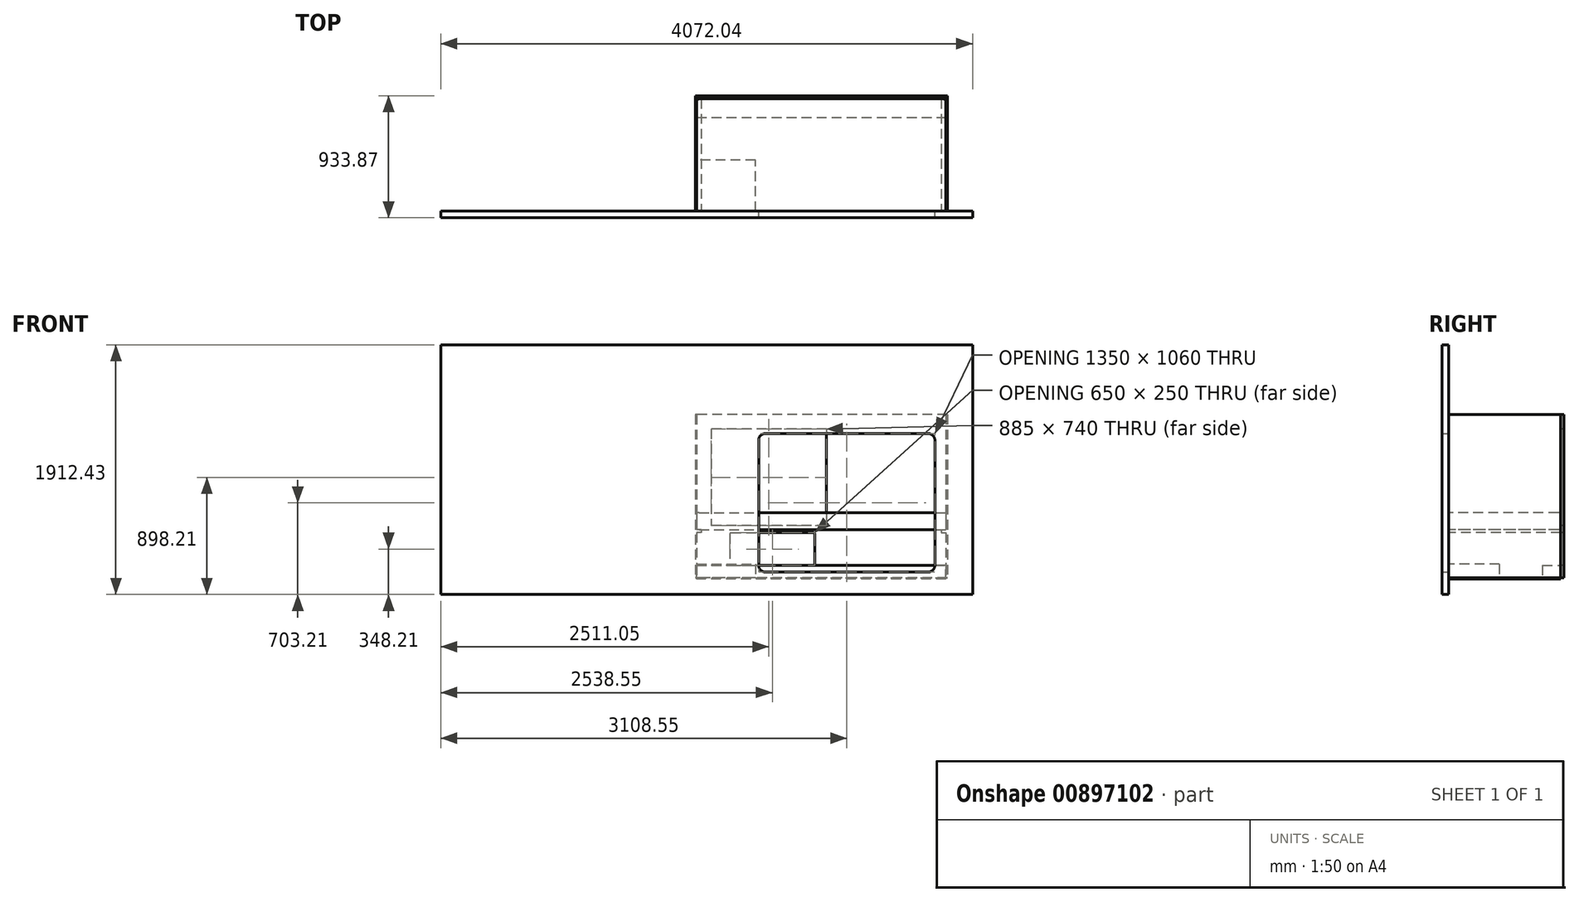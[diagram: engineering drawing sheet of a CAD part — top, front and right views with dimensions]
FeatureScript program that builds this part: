
annotation { "Feature Type Name" : "Feature", "Feature Type Description" : "" }
export const myFeature = defineFeature(function(context is Context, id is Id, definition is map)
    precondition{}
    {
        {
            var Q0;
            Q0=qCreatedBy(makeId("Top.planeOp"),FACE);
            var sketch = newSketch(context, id + "F0", { "sketchPlane" : qUnion([Q0])});
            skLineSegment(sketch, "E0", {"start": v(0, 0) * mm, "end": v(0, 860) * mm});
            skLineSegment(sketch, "E1", {"start": v(0, 860) * mm, "end": v(-1910, 860) * mm});
            skLineSegment(sketch, "E2", {"start": v(-1910, 860) * mm, "end": v(-1910, 0) * mm});
            skLineSegment(sketch, "E3", {"start": v(-1910, 0) * mm, "end": v(0, 0) * mm});
            skLineSegment(sketch, "E4.bottom", {"start": v(0, 0) * mm, "end": v(10, 0) * mm});
            skLineSegment(sketch, "E4.top", {"start": v(0, 860) * mm, "end": v(10, 860) * mm});
            skLineSegment(sketch, "E4.right", {"start": v(10, 0) * mm, "end": v(10, 860) * mm});
            skLineSegment(sketch, "E5.bottom", {"start": v(-1910, 860) * mm, "end": v(-1920, 860) * mm});
            skLineSegment(sketch, "E5.top", {"start": v(-1910, 0) * mm, "end": v(-1920, 0) * mm});
            skLineSegment(sketch, "E5.right", {"start": v(-1920, 860) * mm, "end": v(-1920, 0) * mm});
            skSolve(sketch);
        }
        {
            var Q0;
            Q0=makeQuery(id+"F0.imprint","IMPRINT",FACE,{"disambiguationData":[TD([[makeQuery(id+"F0.imprint","IMPRINT",EDGE,{"derivedFrom":sQuery(id+"F0.wireOp",EDGE,"E1")}),1.0]])]});
            extrude(context, id + "F1", {"entities" : qUnion([Q0]), "oppositeDirection" : true, "depth" : 10 * mm, "offsetDistance" : 25 * mm});
        }
        {
            var Q0;
            Q0=makeQuery(id+"F0.imprint","IMPRINT",FACE,{"disambiguationData":[TD([[makeQuery(id+"F0.imprint","IMPRINT",EDGE,{"derivedFrom":sQuery(id+"F0.wireOp",EDGE,"E1")}),1.0]])]});
            var sketch = newSketch(context, id + "F2", { "sketchPlane" : qUnion([Q0])});
            skLineSegment(sketch, "E6", {"start": v(-1460, 0) * mm, "end": v(-1460, 390) * mm});
            skLineSegment(sketch, "E7", {"start": v(-1460, 390) * mm, "end": v(-1910, 390) * mm});
            skLineSegment(sketch, "E8", {"start": v(-1910, 390) * mm, "end": v(-1910, 0) * mm});
            skLineSegment(sketch, "E9", {"start": v(-1910, 0) * mm, "end": v(-1460, 0) * mm});
            skLineSegment(sketch, "E10.bottom", {"start": v(-1910, 860) * mm, "end": v(0, 860) * mm});
            skLineSegment(sketch, "E10.top", {"start": v(-1910, 720) * mm, "end": v(0, 720) * mm});
            skLineSegment(sketch, "E10.left", {"start": v(-1910, 860) * mm, "end": v(-1910, 720) * mm});
            skLineSegment(sketch, "E10.right", {"start": v(0, 860) * mm, "end": v(0, 720) * mm});
            skSolve(sketch);
        }
        {
            var Q0;
            Q0=makeQuery(id+"F2.imprint","IMPRINT",FACE,{"disambiguationData":[TD([[makeQuery(id+"F2.imprint","IMPRINT",EDGE,{"derivedFrom":sQuery(id+"F2.wireOp",EDGE,"E6")}),1.0]])]});
            extrude(context, id + "F3", {"entities" : qUnion([Q0]), "operationType" : NewBodyOperationType.ADD, "depth" : 105 * mm, "offsetDistance" : 25 * mm});
        }
        {
            var Q0;
            Q0=makeQuery(id+"F2.imprint","IMPRINT",FACE,{"disambiguationData":[TD([[makeQuery(id+"F2.imprint","IMPRINT",EDGE,{"derivedFrom":sQuery(id+"F2.wireOp",EDGE,"E10.bottom")}),1.0]])]});
            extrude(context, id + "F4", {"entities" : qUnion([Q0]), "operationType" : NewBodyOperationType.ADD, "depth" : 95 * mm, "offsetDistance" : 25 * mm});
        }
        {
            var Q0;
            Q0=makeQuery(id+"F0.imprint","IMPRINT",FACE,{"disambiguationData":[TD([[makeQuery(id+"F0.imprint","IMPRINT",EDGE,{"derivedFrom":sQuery(id+"F0.wireOp",EDGE,"E4.bottom")}),1.0]])]});
            extrude(context, id + "F5", {"entities" : qUnion([Q0]), "depth" : 1250 * mm, "offsetDistance" : 25 * mm});
        }
        {
            var Q0;
            Q0=makeQuery(id+"F0.imprint","IMPRINT",FACE,{"disambiguationData":[TD([[makeQuery(id+"F0.imprint","IMPRINT",EDGE,{"derivedFrom":sQuery(id+"F0.wireOp",EDGE,"E5.bottom")}),1.0]])]});
            extrude(context, id + "F6", {"entities" : qUnion([Q0]), "depth" : 1250 * mm, "offsetDistance" : 25 * mm});
        }
        {
            var Q0;
            Q0=makeQuery(id+"F5.opExtrude","SWEPT_FACE",FACE,{"disambiguationData":[OSD([sQuery(id+"F0.wireOp",EDGE,"E0")])]});
            var sketch = newSketch(context, id + "F7", { "sketchPlane" : qUnion([Q0])});
            skLineSegment(sketch, "E11.bottom", {"start": v(-860, 345) * mm, "end": v(0, 345) * mm});
            skLineSegment(sketch, "E11.top", {"start": v(-860, 370) * mm, "end": v(0, 370) * mm});
            skLineSegment(sketch, "E11.left", {"start": v(-860, 345) * mm, "end": v(-860, 370) * mm});
            skLineSegment(sketch, "E11.right", {"start": v(0, 345) * mm, "end": v(0, 370) * mm});
            skSolve(sketch);
        }
        {
            var Q0;
            Q0=makeQuery(id+"F7.imprint","IMPRINT",FACE,{"disambiguationData":[TD([[makeQuery(id+"F7.imprint","IMPRINT",EDGE,{"derivedFrom":sQuery(id+"F7.wireOp",EDGE,"E11.bottom")}),1.0]])]});
            extrude(context, id + "F8", {"entities" : qUnion([Q0]), "operationType" : NewBodyOperationType.ADD, "depth" : 35 * mm, "offsetDistance" : 25 * mm});
        }
        {
            var Q0;
            Q0=makeQuery(id+"F6.opExtrude","SWEPT_FACE",FACE,{"disambiguationData":[OSD([sQuery(id+"F0.wireOp",EDGE,"E2")])]});
            var sketch = newSketch(context, id + "F9", { "sketchPlane" : qUnion([Q0])});
            skLineSegment(sketch, "E12.bottom", {"start": v(860, 345) * mm, "end": v(0, 345) * mm});
            skLineSegment(sketch, "E12.top", {"start": v(860, 370) * mm, "end": v(0, 370) * mm});
            skLineSegment(sketch, "E12.left", {"start": v(860, 345) * mm, "end": v(860, 370) * mm});
            skLineSegment(sketch, "E12.right", {"start": v(0, 345) * mm, "end": v(0, 370) * mm});
            skSolve(sketch);
        }
        {
            var Q0;
            Q0=makeQuery(id+"F9.imprint","IMPRINT",FACE,{"disambiguationData":[TD([[makeQuery(id+"F9.imprint","IMPRINT",EDGE,{"derivedFrom":sQuery(id+"F9.wireOp",EDGE,"E12.bottom")}),-1.0]])]});
            extrude(context, id + "F10", {"entities" : qUnion([Q0]), "operationType" : NewBodyOperationType.ADD, "depth" : 35 * mm, "offsetDistance" : 25 * mm});
        }
        {
            var Q0;
            Q0=qCreatedBy(makeId("Top.planeOp"),FACE);
            var sketch = newSketch(context, id + "F11", { "sketchPlane" : qUnion([Q0])});
            skLineSegment(sketch, "E13.bottom", {"start": v(10, 860) * mm, "end": v(-1920, 860) * mm});
            skLineSegment(sketch, "E13.top", {"start": v(10, 883.87) * mm, "end": v(-1920, 883.87) * mm});
            skLineSegment(sketch, "E13.left", {"start": v(10, 860) * mm, "end": v(10, 883.87) * mm});
            skLineSegment(sketch, "E13.right", {"start": v(-1920, 860) * mm, "end": v(-1920, 883.87) * mm});
            skSolve(sketch);
        }
        {
            var Q0;
            Q0=makeQuery(id+"F11.imprint","IMPRINT",FACE,{"disambiguationData":[TD([[makeQuery(id+"F11.imprint","IMPRINT",EDGE,{"derivedFrom":sQuery(id+"F11.wireOp",EDGE,"E13.bottom")}),-1.0]])]});
            extrude(context, id + "F12", {"entities" : qUnion([Q0]), "depth" : 1250 * mm, "offsetDistance" : 25 * mm});
        }
        {
            var Q0;
            Q0=makeQuery(id+"F12.opExtrude","SWEPT_FACE",FACE,{"disambiguationData":[OSD([sQuery(id+"F11.wireOp",EDGE,"E13.bottom")])]});
            var sketch = newSketch(context, id + "F13", { "sketchPlane" : qUnion([Q0])});
            skLineSegment(sketch, "E14.bottom", {"start": v(-1645, 345) * mm, "end": v(-1015, 345) * mm});
            skLineSegment(sketch, "E14.top", {"start": v(-1645, 95) * mm, "end": v(-1015, 95) * mm});
            skLineSegment(sketch, "E14.left", {"start": v(-1655, 335) * mm, "end": v(-1655, 105) * mm});
            skLineSegment(sketch, "E14.right", {"start": v(-1005, 335) * mm, "end": v(-1005, 105) * mm});
            skPoint(sketch, "E15.visualSharp", {"position": v(-1655, 345) * mm});
            skArc(sketch, "E15.filletArc", {"start": v(-1645, 345) * mm, "mid": v(-1652.07, 342.07) * mm, "end": v(-1655, 335) * mm});
            skPoint(sketch, "E16.visualSharp", {"position": v(-1655, 95) * mm});
            skArc(sketch, "E16.filletArc", {"start": v(-1655, 105) * mm, "mid": v(-1652.07, 97.93) * mm, "end": v(-1645, 95) * mm});
            skPoint(sketch, "E17.visualSharp", {"position": v(-1005, 345) * mm});
            skArc(sketch, "E17.filletArc", {"start": v(-1005, 335) * mm, "mid": v(-1007.93, 342.07) * mm, "end": v(-1015, 345) * mm});
            skPoint(sketch, "E18.visualSharp", {"position": v(-1005, 95) * mm});
            skArc(sketch, "E18.filletArc", {"start": v(-1015, 95) * mm, "mid": v(-1007.93, 97.93) * mm, "end": v(-1005, 105) * mm});
            skLineSegment(sketch, "E19.bottom", {"start": v(-915, 1140) * mm, "end": v(-1800, 1140) * mm});
            skLineSegment(sketch, "E19.top", {"start": v(-915, 400) * mm, "end": v(-1800, 400) * mm});
            skLineSegment(sketch, "E19.left", {"start": v(-915, 1140) * mm, "end": v(-915, 400) * mm});
            skLineSegment(sketch, "E19.right", {"start": v(-1800, 1140) * mm, "end": v(-1800, 400) * mm});
            skSolve(sketch);
        }
        {
            var Q0;
            Q0=makeQuery(id+"F13.imprint","IMPRINT",FACE,{"disambiguationData":[TD([[makeQuery(id+"F13.imprint","IMPRINT",EDGE,{"derivedFrom":sQuery(id+"F13.wireOp",EDGE,"E14.bottom")}),-1.0]])]});
            extrude(context, id + "F14", {"entities" : qUnion([Q0]), "operationType" : NewBodyOperationType.REMOVE, "oppositeDirection" : true, "depth" : 219 * mm, "offsetDistance" : 25 * mm});
        }
        {
            var Q0;
            Q0=makeQuery(id+"F13.imprint","IMPRINT",FACE,{"disambiguationData":[TD([[makeQuery(id+"F13.imprint","IMPRINT",EDGE,{"derivedFrom":sQuery(id+"F13.wireOp",EDGE,"E19.bottom")}),1.0]])]});
            extrude(context, id + "F15", {"entities" : qUnion([Q0]), "operationType" : NewBodyOperationType.REMOVE, "oppositeDirection" : true, "depth" : 210 * mm, "offsetDistance" : 25 * mm});
        }
        {
            var Q0;
            Q0=makeQuery(id+"F10.opExtrude","SWEPT_FACE",FACE,{"disambiguationData":[OSD([sQuery(id+"F9.wireOp",EDGE,"E12.top")])]});
            var sketch = newSketch(context, id + "F16", { "sketchPlane" : qUnion([Q0])});
            skLineSegment(sketch, "E20.bottom", {"start": v(-1890, 860) * mm, "end": v(-20, 860) * mm});
            skLineSegment(sketch, "E20.top", {"start": v(-1890, 0) * mm, "end": v(-20, 0) * mm});
            skLineSegment(sketch, "E20.left", {"start": v(-1910, 840) * mm, "end": v(-1910, 20) * mm});
            skLineSegment(sketch, "E20.right", {"start": v(0, 840) * mm, "end": v(0, 20) * mm});
            skPoint(sketch, "E21.visualSharp", {"position": v(0, 860) * mm});
            skArc(sketch, "E21.filletArc", {"start": v(0, 840) * mm, "mid": v(-5.86, 854.14) * mm, "end": v(-20, 860) * mm});
            skPoint(sketch, "E22.visualSharp", {"position": v(0, 0) * mm});
            skArc(sketch, "E22.filletArc", {"start": v(-20, 0) * mm, "mid": v(-5.86, 5.86) * mm, "end": v(0, 20) * mm});
            skPoint(sketch, "E23.visualSharp", {"position": v(-1910, 860) * mm});
            skArc(sketch, "E23.filletArc", {"start": v(-1890, 860) * mm, "mid": v(-1904.14, 854.14) * mm, "end": v(-1910, 840) * mm});
            skPoint(sketch, "E24.visualSharp", {"position": v(-1910, 0) * mm});
            skArc(sketch, "E24.filletArc", {"start": v(-1910, 20) * mm, "mid": v(-1904.14, 5.86) * mm, "end": v(-1890, 0) * mm});
            skSolve(sketch);
        }
        {
            var Q0;
            Q0 = qSketchRegion(id + "F16", true);
            extrude(context, id + "F17", {"entities" : qUnion([Q0]), "depth" : 130 * mm, "offsetDistance" : 25 * mm});
        }
        {
            var Q0;
            Q0=qCreatedBy(makeId("Front.planeOp"),FACE);
            var sketch = newSketch(context, id + "F18", { "sketchPlane" : qUnion([Q0])});
            skLineSegment(sketch, "E25.bottom", {"start": v(203.49, -128.21) * mm, "end": v(-3868.55, -128.21) * mm});
            skLineSegment(sketch, "E25.top", {"start": v(203.49, 1784.22) * mm, "end": v(-3868.55, 1784.22) * mm});
            skLineSegment(sketch, "E25.left", {"start": v(203.49, -128.21) * mm, "end": v(203.49, 1784.22) * mm});
            skLineSegment(sketch, "E25.right", {"start": v(-3868.55, -128.21) * mm, "end": v(-3868.55, 1784.22) * mm});
            skSolve(sketch);
        }
        {
            var Q0;
            Q0=makeQuery(id+"F18.imprint","IMPRINT",FACE,{"disambiguationData":[TD([[makeQuery(id+"F18.imprint","IMPRINT",EDGE,{"derivedFrom":sQuery(id+"F18.wireOp",EDGE,"E25.bottom")}),-1.0]])]});
            extrude(context, id + "F19", {"entities" : qUnion([Q0]), "depth" : 50 * mm, "offsetDistance" : 25 * mm});
        }
        {
            var Q0;
            Q0=makeQuery(id+"F19.opExtrude","CAP_FACE",FACE,{"disambiguationData":[OSD([sQuery(id+"F18.wireOp",EDGE,"E25.bottom"),sQuery(id+"F18.wireOp",EDGE,"E25.top"),sQuery(id+"F18.wireOp",EDGE,"E25.left"),sQuery(id+"F18.wireOp",EDGE,"E25.right")])],"isStart":true});
            var sketch = newSketch(context, id + "F20", { "sketchPlane" : qUnion([Q0])});
            skLineSegment(sketch, "E26.bottom", {"start": v(135, 1105) * mm, "end": v(1385, 1105) * mm});
            skLineSegment(sketch, "E26.top", {"start": v(135, 45) * mm, "end": v(1385, 45) * mm});
            skLineSegment(sketch, "E26.left", {"start": v(85, 1055) * mm, "end": v(85, 95) * mm});
            skLineSegment(sketch, "E26.right", {"start": v(1435, 1055) * mm, "end": v(1435, 95) * mm});
            skPoint(sketch, "E27.visualSharp", {"position": v(85, 1105) * mm});
            skArc(sketch, "E27.filletArc", {"start": v(135, 1105) * mm, "mid": v(99.64, 1090.36) * mm, "end": v(85, 1055) * mm});
            skPoint(sketch, "E28.visualSharp", {"position": v(1435, 1105) * mm});
            skArc(sketch, "E28.filletArc", {"start": v(1435, 1055) * mm, "mid": v(1420.36, 1090.36) * mm, "end": v(1385, 1105) * mm});
            skPoint(sketch, "E29.visualSharp", {"position": v(85, 45) * mm});
            skArc(sketch, "E29.filletArc", {"start": v(85, 95) * mm, "mid": v(99.64, 59.64) * mm, "end": v(135, 45) * mm});
            skPoint(sketch, "E30.visualSharp", {"position": v(1435, 45) * mm});
            skArc(sketch, "E30.filletArc", {"start": v(1385, 45) * mm, "mid": v(1420.36, 59.64) * mm, "end": v(1435, 95) * mm});
            skSolve(sketch);
        }
        {
            var Q0;
            Q0=makeQuery(id+"F20.imprint","IMPRINT",FACE,{"disambiguationData":[TD([[makeQuery(id+"F20.imprint","IMPRINT",EDGE,{"derivedFrom":sQuery(id+"F20.wireOp",EDGE,"E26.bottom")}),-1.0]])]});
            extrude(context, id + "F21", {"entities" : qUnion([Q0]), "operationType" : NewBodyOperationType.REMOVE, "oppositeDirection" : true, "depth" : 620 * mm, "offsetDistance" : 25 * mm});
        }
    });
